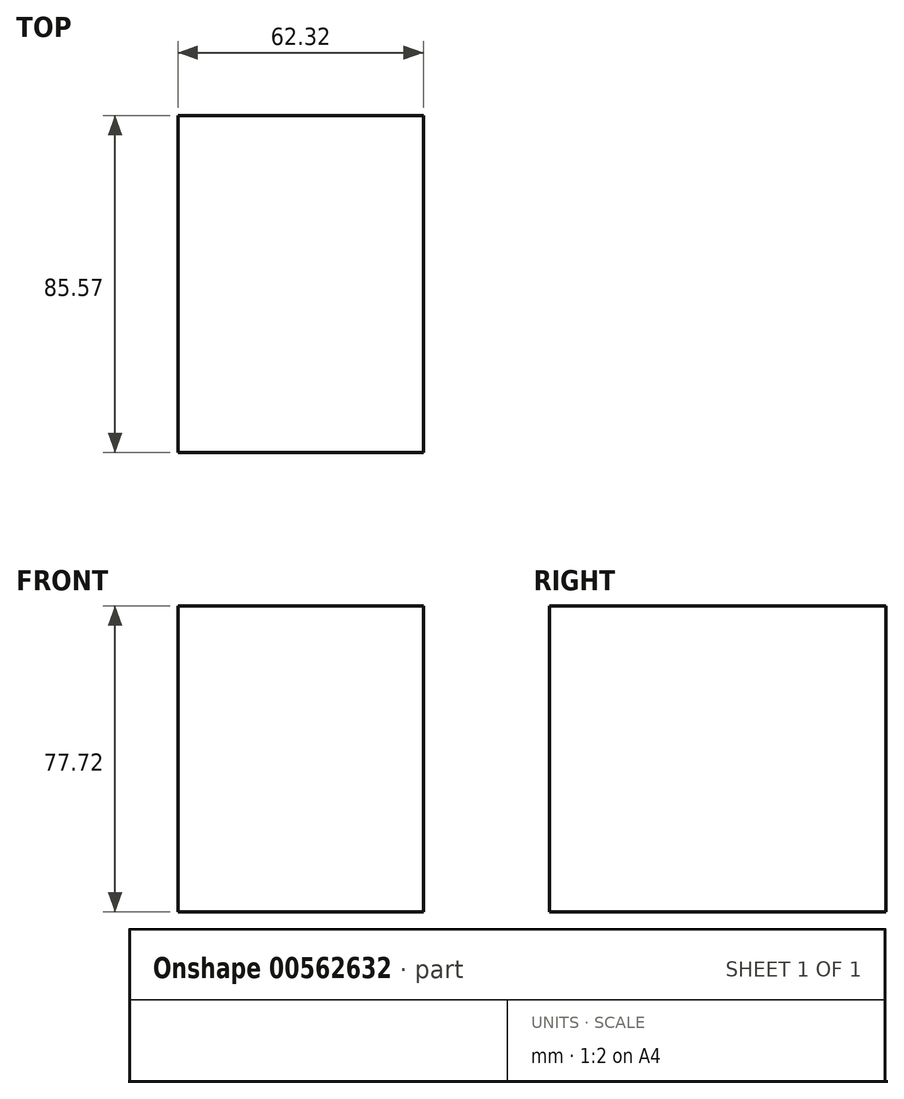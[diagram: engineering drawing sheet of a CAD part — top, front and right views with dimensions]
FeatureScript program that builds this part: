
annotation { "Feature Type Name" : "Feature", "Feature Type Description" : "" }
export const myFeature = defineFeature(function(context is Context, id is Id, definition is map)
    precondition{}
    {
        {
            var Q0;
            Q0=qCreatedBy(makeId("Top.planeOp"),FACE);
            var sketch = newSketch(context, id + "F0", { "sketchPlane" : qUnion([Q0])});
            skLineSegment(sketch, "E0.bottom", {"start": v(-151.55, 26.63) * mm, "end": v(-89.23, 26.63) * mm});
            skLineSegment(sketch, "E0.top", {"start": v(-151.55, -58.94) * mm, "end": v(-89.23, -58.94) * mm});
            skLineSegment(sketch, "E0.left", {"start": v(-151.55, 26.63) * mm, "end": v(-151.55, -58.94) * mm});
            skLineSegment(sketch, "E0.right", {"start": v(-89.23, 26.63) * mm, "end": v(-89.23, -58.94) * mm});
            skLineSegment(sketch, "E1.bottom", {"start": v(-89.23, -58.94) * mm, "end": v(-137.43, -58.94) * mm});
            skLineSegment(sketch, "E1.top", {"start": v(-89.23, 7.43) * mm, "end": v(-137.43, 7.43) * mm});
            skLineSegment(sketch, "E1.left", {"start": v(-89.23, -58.94) * mm, "end": v(-89.23, 7.43) * mm});
            skLineSegment(sketch, "E1.right", {"start": v(-137.43, -58.94) * mm, "end": v(-137.43, 7.43) * mm});
            skSolve(sketch);
        }
        {
            var Q0;
            Q0 = qSketchRegion(id + "F0", true);
            extrude(context, id + "F1", {"entities" : qUnion([Q0]), "depth" : 77.72 * mm, "offsetDistance" : 25.4 * mm});
        }
    });
